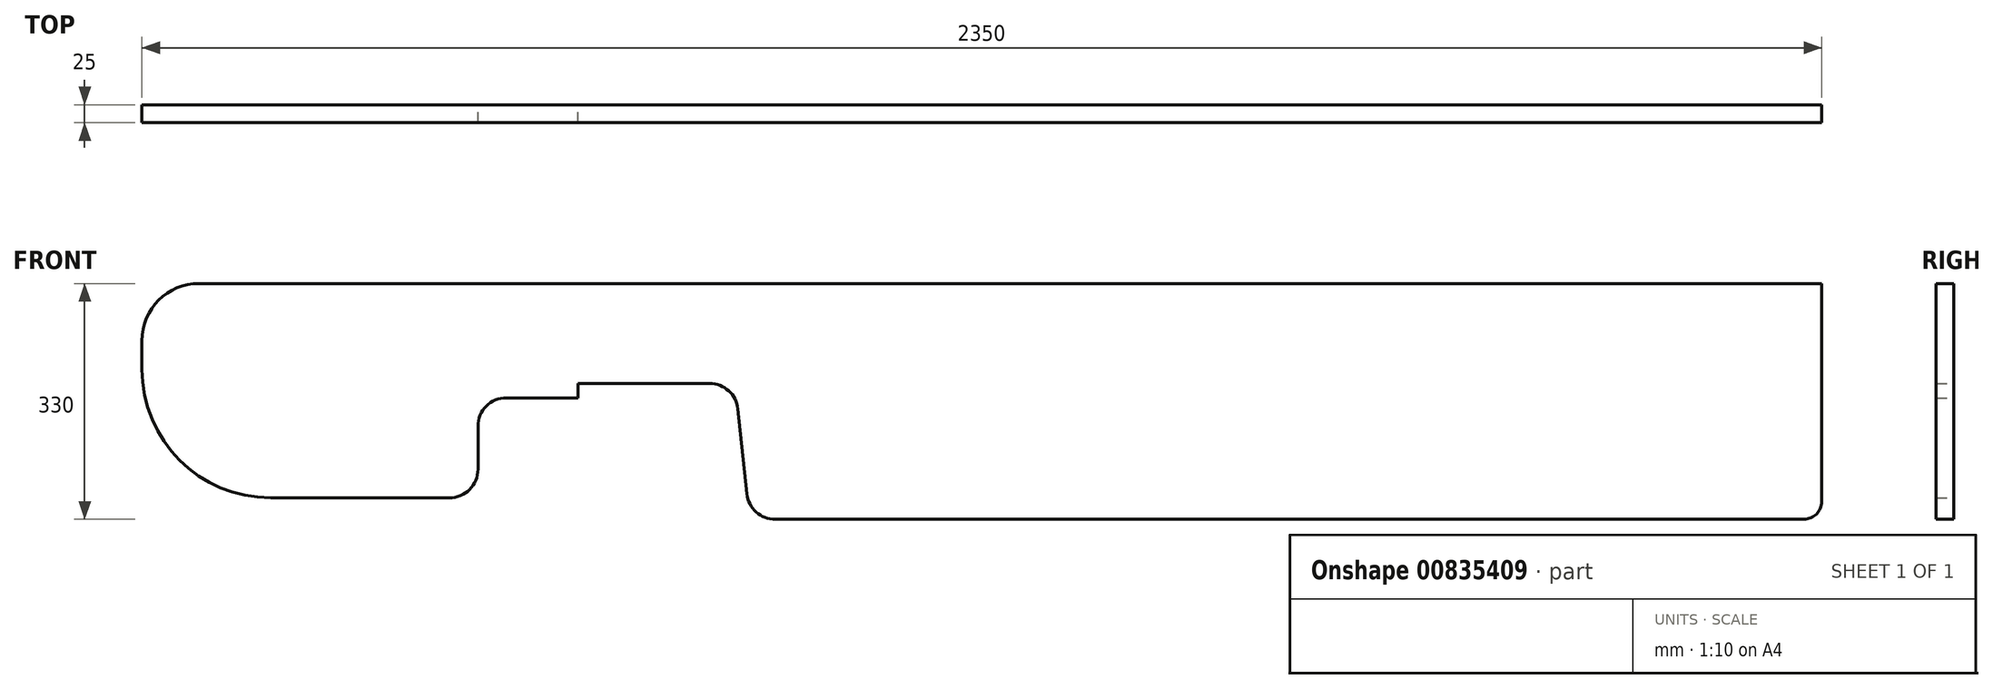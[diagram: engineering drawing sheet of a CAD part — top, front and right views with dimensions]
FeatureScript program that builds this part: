
annotation { "Feature Type Name" : "Feature", "Feature Type Description" : "" }
export const myFeature = defineFeature(function(context is Context, id is Id, definition is map)
    precondition{}
    {
        {
            var Q0;
            Q0=qCreatedBy(makeId("Front.planeOp"),FACE);
            var sketch = newSketch(context, id + "F0", { "sketchPlane" : qUnion([Q0])});
            skLineSegment(sketch, "E0.top", {"start": v(0, 330) * mm, "end": v(-2270, 330) * mm});
            skLineSegment(sketch, "E0.left", {"start": v(0, 25) * mm, "end": v(0, 330) * mm});
            skLineSegment(sketch, "E1", {"start": v(-1503.77, 35.81) * mm, "end": v(-1516.23, 154.19) * mm});
            skLineSegment(sketch, "E2", {"start": v(-1556.01, 190) * mm, "end": v(-1740, 190) * mm});
            skLineSegment(sketch, "E3", {"start": v(-1740, 190) * mm, "end": v(-1740, 170) * mm});
            skPoint(sketch, "E4.visualSharp", {"position": v(0, 330) * mm});
            skLineSegment(sketch, "E4.filletArc", {"start": v(0, 330) * mm, "end": v(0, 330) * mm});
            skPoint(sketch, "E5.visualSharp", {"position": v(0, 0) * mm});
            skArc(sketch, "E5.filletArc", {"start": v(-25, 0) * mm, "mid": v(-7.32, 7.32) * mm, "end": v(0, 25) * mm});
            skLineSegment(sketch, "E6", {"start": v(-1463.99, 0) * mm, "end": v(-25, 0) * mm});
            skPoint(sketch, "E7.visualSharp", {"position": v(-1500, 0) * mm});
            skArc(sketch, "E7.filletArc", {"start": v(-1503.77, 35.81) * mm, "mid": v(-1490.75, 10.27) * mm, "end": v(-1463.99, 0) * mm});
            skPoint(sketch, "E8.visualSharp", {"position": v(-1520, 190) * mm});
            skArc(sketch, "E8.filletArc", {"start": v(-1516.23, 154.19) * mm, "mid": v(-1529.25, 179.73) * mm, "end": v(-1556.01, 190) * mm});
            skLineSegment(sketch, "E9", {"start": v(-1740, 170) * mm, "end": v(-1840, 170) * mm});
            skLineSegment(sketch, "E10", {"start": v(-1880, 130) * mm, "end": v(-1880, 70) * mm});
            skLineSegment(sketch, "E11", {"start": v(-1920, 30) * mm, "end": v(-2170, 30) * mm});
            skLineSegment(sketch, "E12", {"start": v(-2350, 210) * mm, "end": v(-2350, 250) * mm});
            skPoint(sketch, "E13.visualSharp", {"position": v(-2350, 30) * mm});
            skArc(sketch, "E13.filletArc", {"start": v(-2350, 210) * mm, "mid": v(-2297.28, 82.72) * mm, "end": v(-2170, 30) * mm});
            skPoint(sketch, "E14.visualSharp", {"position": v(-2350, 330) * mm});
            skArc(sketch, "E14.filletArc", {"start": v(-2270, 330) * mm, "mid": v(-2326.57, 306.57) * mm, "end": v(-2350, 250) * mm});
            skPoint(sketch, "E15.visualSharp", {"position": v(-1880, 30) * mm});
            skArc(sketch, "E15.filletArc", {"start": v(-1920, 30) * mm, "mid": v(-1891.72, 41.72) * mm, "end": v(-1880, 70) * mm});
            skPoint(sketch, "E16.visualSharp", {"position": v(-1880, 170) * mm});
            skArc(sketch, "E16.filletArc", {"start": v(-1840, 170) * mm, "mid": v(-1868.28, 158.28) * mm, "end": v(-1880, 130) * mm});
            skSolve(sketch);
        }
        {
            var Q0;
            Q0=makeQuery(id+"F0.imprint","IMPRINT",FACE,{"disambiguationData":[TD([[makeQuery(id+"F0.imprint","IMPRINT",EDGE,{"derivedFrom":sQuery(id+"F0.wireOp",EDGE,"E0.top")}),1.0]])]});
            extrude(context, id + "F1", {"entities" : qUnion([Q0]), "depth" : 25 * mm, "offsetDistance" : 25 * mm});
        }
    });
